# Revit family: GRAS_HW-19N-20-30 SF
name_source: partatom
category: Osprzęt hydrauliczny
revit_build: Autodesk Revit 2018 (Build: 20190510_1515(x64)
units: mm (PartAtom-declared; Revit-internal decimal feet)

## family parameters
Obiekt nadrzędny = Powierzchnia
Punkt obliczania pomieszczeń = Nie
Tnij formami wycięć po wczytaniu = Nie
Typ części = Normalny
Współdzielony = Nie
Wymiar okrągłego złącza = Użyj średnicy

## types (2) — shared parameters
Cabinet depth = 180 mm  [stored 0.590551 ft]
Cabinet height = 895 mm  [stored 2.93635 ft]
Cabinet width = 795 mm  [stored 2.60827 ft]
D1 = 40 mm  [stored 0.131234 ft]
D2 = 40 mm  [stored 0.131234 ft]
DN = 19 mm  [stored 0.062336 ft]
Flow = 35.0 L/s
H1 = 40 mm  [stored 0.131234 ft]
K Factor = 42
Mounting_Height = 3000 mm  [stored 9.84252 ft]
Opis = https://gras.pl
Producent = GRAS PPPH
URL = http://www.gras.pl
W1 = 40 mm  [stored 0.131234 ft]
W2 = 40 mm  [stored 0.131234 ft]
zero-valued in all types: Domyślna rzędna

## per-type parameters (varying)
| type | Cabinet material | Model |
| HWA-19N-20/30 SF, RAL9010 | DC01, RAL9010 | HWA-19N-20/30 SF, RAL9010 |
| HWA-19N-20/30 SF, RAL3000 | DC01, RAL3000 | HWA-19N-20/30 SF, RAL 3000 |

note: [stored X ft] marks values corroborated as IEEE doubles in the binary element streams (Revit-internal decimal feet)

## geometry (parser evidence)
native form markers: Blend x8
no freeform markers — native parametric forms only
